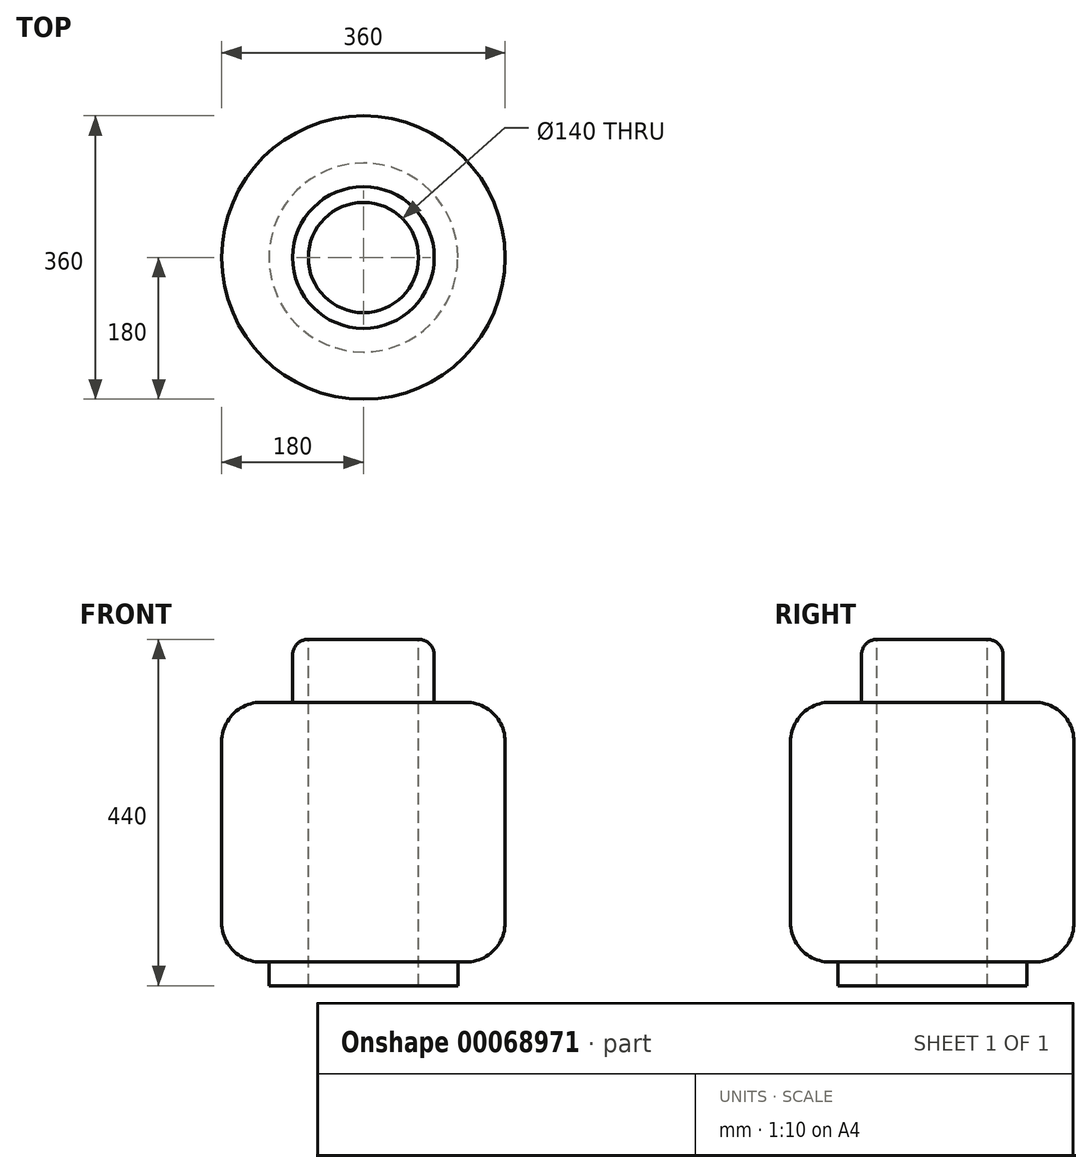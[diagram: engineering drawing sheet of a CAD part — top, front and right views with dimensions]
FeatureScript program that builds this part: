
annotation { "Feature Type Name" : "Feature", "Feature Type Description" : "" }
export const myFeature = defineFeature(function(context is Context, id is Id, definition is map)
    precondition{}
    {
        {
            var Q0;
            Q0=qCreatedBy(makeId("Front.planeOp"),FACE);
            var sketch = newSketch(context, id + "F0", { "sketchPlane" : qUnion([Q0])});
            skLineSegment(sketch, "E0", {"start": v(0, 440) * mm, "end": v(70, 440) * mm});
            skLineSegment(sketch, "E1", {"start": v(90, 420) * mm, "end": v(90, 360) * mm});
            skLineSegment(sketch, "E2", {"start": v(90, 360) * mm, "end": v(130, 360) * mm});
            skLineSegment(sketch, "E3", {"start": v(180, 310) * mm, "end": v(180, 80) * mm});
            skLineSegment(sketch, "E4", {"start": v(130, 30) * mm, "end": v(120, 30) * mm});
            skLineSegment(sketch, "E5", {"start": v(120, 30) * mm, "end": v(120, 0) * mm});
            skLineSegment(sketch, "E6", {"start": v(120, 0) * mm, "end": v(0, 0) * mm});
            skLineSegment(sketch, "E7", {"start": v(0, 440) * mm, "end": v(0, 0) * mm});
            skPoint(sketch, "E8.visualSharp", {"position": v(180, 360) * mm});
            skArc(sketch, "E8.filletArc", {"start": v(180, 310) * mm, "mid": v(165.36, 345.36) * mm, "end": v(130, 360) * mm});
            skPoint(sketch, "E9.visualSharp", {"position": v(180, 30) * mm});
            skArc(sketch, "E9.filletArc", {"start": v(130, 30) * mm, "mid": v(165.36, 44.64) * mm, "end": v(180, 80) * mm});
            skPoint(sketch, "E10.visualSharp", {"position": v(90, 440) * mm});
            skArc(sketch, "E10.filletArc", {"start": v(90, 420) * mm, "mid": v(84.14, 434.14) * mm, "end": v(70, 440) * mm});
            skSolve(sketch);
        }
        {
            var Q0;
            Q0=makeQuery(id+"F0.imprint","IMPRINT",FACE,{"disambiguationData":[TD([[makeQuery(id+"F0.imprint","IMPRINT",EDGE,{"derivedFrom":sQuery(id+"F0.wireOp",EDGE,"E0")}),-1.0]])]});
            var Q1;
            Q1=sQuery(id+"F0.wireOp",EDGE,"E7");
            revolve(context, id + "F1", {"entities" : qUnion([Q0]), "axis" : qUnion([Q1]), "revolveType" : RevolveType.FULL});
        }
        {
            var Q0;
            Q0=makeQuery(id+"F1.opRevolve","SWEPT_FACE",FACE,{"disambiguationData":[OSD([sQuery(id+"F0.wireOp",EDGE,"E0")])]});
            var sketch = newSketch(context, id + "F2", { "sketchPlane" : qUnion([Q0])});
            skCircle(sketch, "E11", {"center": v(0, 0) * mm, "radius": 75 * mm});
            skSolve(sketch);
        }
        {
            var Q0;
            Q0=makeQuery(id+"F2.imprint","IMPRINT",FACE,{"disambiguationData":[TD([[makeQuery(id+"F2.imprint","IMPRINT",EDGE,{"derivedFrom":makeQuery(id+"F1.opRevolve","SWEPT_EDGE",EDGE,{"disambiguationData":[OSD([sQuery(id+"F0.wireOp",EDGE,"E0"),sQuery(id+"F0.wireOp",EDGE,"E10.filletArc")])]})}),1.0]])]});
            extrude(context, id + "F3", {"entities" : qUnion([Q0]), "operationType" : NewBodyOperationType.REMOVE, "oppositeDirection" : true, "depth" : 500 * mm});
        }
    });
